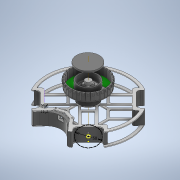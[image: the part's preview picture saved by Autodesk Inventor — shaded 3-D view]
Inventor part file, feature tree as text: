
AUTODESK INVENTOR PART (.ipt)
format: ipt  version: 2020 (Build 240168000, 168)  size: 2,077,184 bytes
history: native  units: mm
features: sketch x21, extrude x19, other x13, projected_geometry x4, pattern_circular x2, revolve x1
ambient origin geometry x8: Origin, YZ Plane, XZ Plane, XY Plane, X Axis, Y Axis, Z Axis, Center Point
bodies: Body1 (feature_tree)
feature tree (60):
  other  "Твердое тело1"
  other  "bottom_frame"
  other  "motowheels"
  extrude  "catcher"  Depth=88.0mm
  sketch  "Эскиз4"
  extrude  "Выдавливание2"  Depth=7.0mm
  extrude  "Выдавливание3"  Depth=5.0mm
  extrude  "Выдавливание21"  Depth=7.0mm
  other  "РабПлоскость1"
  extrude  "Выдавливание6"  Depth=5.0mm
  sketch  "Эскиз8"
  other  "РабПлоскость2"
  sketch  "Эскиз11"
  sketch  "Эскиз12"
  other  "РабПлоскость3"
  sketch  "Эскиз18"
  sketch  "Эскиз19"
  extrude  "Выдавливание15"  Depth=7.0mm
  extrude  "Выдавливание16"  Depth=5.0mm
  other  "РабПлоскость7"
  sketch  "Эскиз22"
  other  "РабПлоскость9"
  sketch  "Эскиз25"
  other  "РабПлоскость10"
  revolve  "Вращение2"
  sketch  "Эскиз29"
  extrude  "Выдавливание20"  Depth=5.1mm
  pattern_circular  "Круговой массив3"  Count=3  [1 undecoded]
  other  "РабПлоскость11"
  extrude  "Выдавливание22"  Depth=7.5mm
  other  "upper_frame"
  sketch  "Эскиз33"
  extrude  "Выдавливание23"  Depth=11.2mm
  sketch  "Эскиз34"
  other  "РабПлоскость12"
  extrude  "Выдавливание24"  Depth=20.5mm
  sketch  "Эскиз36"
  extrude  "Выдавливание25"  Depth=7.0mm TaperAngle=0.0deg
  extrude  "Выдавливание26"  Depth=4.0mm TaperAngle=0.0deg
  extrude  "Выдавливание27"  Depth=7.6mm
  pattern_circular  "Круговой массив4"  [2 undecoded]
  sketch  "Эскиз38"
  extrude  "Выдавливание28"  Depth=10.0mm
  extrude  "Выдавливание29"  Depth=15.0mm
  extrude  "Выдавливание30"  Depth=20.0mm TaperAngle=0.0deg
  sketch  "Эскиз40"
  other  "РабПлоскость13"
  extrude  "Выдавливание32"  Depth=3.0mm
  extrude  "Выдавливание33"  Depth=6.0mm
  sketch  "Эскиз7"
  projected_geometry  "Спроецированная петля1"
  sketch  "Эскиз26"
  projected_geometry  "Спроецированная петля2"
  sketch  "Эскиз30"
  projected_geometry  "Спроецированная петля3"
  projected_geometry  "Спроецированная петля4"
  sketch  "Эскиз35"
  sketch  "Эскиз37"
  sketch  "Эскиз39"
  sketch  "Эскиз41"
note: 3 required parameter values undecoded (feature->parameter linkage not recoverable at this tier; creation-order binding heuristic only, values carry confidence <= 0.55)
